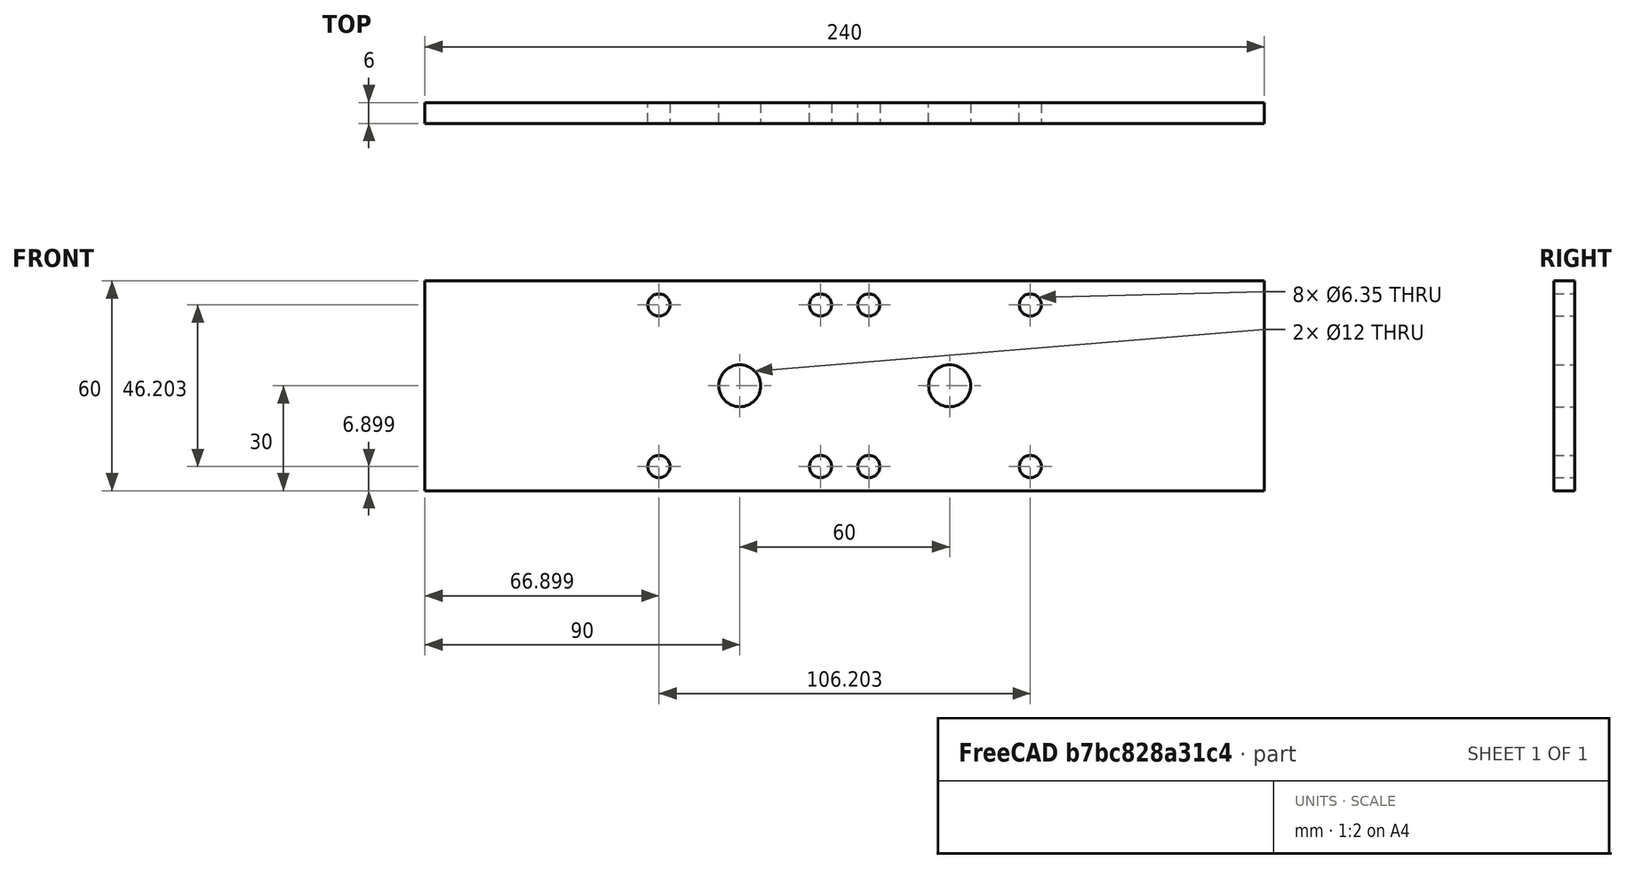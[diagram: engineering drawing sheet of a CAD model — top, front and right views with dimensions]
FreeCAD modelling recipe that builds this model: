
FCSTD DOCUMENT  (FreeCAD 0.18R4 (GitTag))
Label: soporte_motor
License: All rights reserved
LicenseURL: http://en.wikipedia.org/wiki/All_rights_reserved
objects: Sketcher::SketchObject×1, PartDesign::Pad×1, PartDesign::Body×1
note: 4 computed .brp shape members not serialized (recipe doc carries the construction recipe); baked Part::Feature solids carry a one-line shape summary decoded from their .brp

FEATURE [Sketcher::SketchObject] Sketch
  MapMode = 5
  Placement = pos=(0,0,0) rot=(1,0,0;1.5708rad)
  Support = -> [XZ_Plane]
  sketch-geometry (14):
    g0: LineSegment StartX=0 StartY=0 StartZ=0 EndX=240 EndY=0 EndZ=0
    g1: LineSegment StartX=240 StartY=0 StartZ=0 EndX=240 EndY=60 EndZ=0
    g2: LineSegment StartX=240 StartY=60 StartZ=0 EndX=0 EndY=60 EndZ=0
    g3: LineSegment StartX=0 StartY=60 StartZ=0 EndX=0 EndY=0 EndZ=0
    g4: Circle CenterX=90 CenterY=30 CenterZ=0 NormalX=0 NormalY=0 NormalZ=1 AngleXU=0 Radius=6
    g5: Circle CenterX=113.101 CenterY=53.1013 CenterZ=0 NormalX=0 NormalY=0 NormalZ=1 AngleXU=0 Radius=3.175
    g6: Circle CenterX=66.8987 CenterY=53.1013 CenterZ=0 NormalX=0 NormalY=0 NormalZ=1 AngleXU=0 Radius=3.175
    g7: Circle CenterX=66.8987 CenterY=6.8987 CenterZ=0 NormalX=0 NormalY=0 NormalZ=1 AngleXU=0 Radius=3.175
    g8: Circle CenterX=113.101 CenterY=6.8987 CenterZ=0 NormalX=0 NormalY=0 NormalZ=1 AngleXU=0 Radius=3.175
    g9: Circle CenterX=150 CenterY=30 CenterZ=0 NormalX=0 NormalY=0 NormalZ=1 AngleXU=0 Radius=6
    g10: Circle CenterX=173.101 CenterY=53.1013 CenterZ=0 NormalX=0 NormalY=0 NormalZ=1 AngleXU=0 Radius=3.175
    g11: Circle CenterX=126.899 CenterY=53.1013 CenterZ=0 NormalX=0 NormalY=0 NormalZ=1 AngleXU=0 Radius=3.175
    g12: Circle CenterX=126.899 CenterY=6.8987 CenterZ=0 NormalX=0 NormalY=0 NormalZ=1 AngleXU=0 Radius=3.175
    g13: Circle CenterX=173.101 CenterY=6.8987 CenterZ=0 NormalX=0 NormalY=0 NormalZ=1 AngleXU=0 Radius=3.175
  constraints (41):
    c: Coincident(g0,g1)
    c: Coincident(g1,g2)
    c: Coincident(g2,g3)
    c: Coincident(g3,g0)
    c: Horizontal(g0)
    c: Horizontal(g2)
    c: Vertical(g1)
    c: Vertical(g3)
    c: Coincident(g0,g-1)
    c: DistanceX(g0,g0) = 240
    c: DistanceY(g3,g3) = 60
    c: Distance(g4,g2) = 30
    c: Distance(g4,g3) = 90
    c: Radius(g4) = 6
    c: Radius(g5) = 3.175
    c: Radius(g6) = 3.175
    c: Radius(g8) = 3.175
    c: Radius(g7) = 3.175
    c: DistanceX(g7,g8) = 46.2026
    c: DistanceX(g6,g5) = 46.2026
    c: DistanceX(g6,g4) = 23.1013
    c: DistanceX(g7,g4) = 23.1013
    c: DistanceY(g8,g5) = 46.2026
    c: DistanceY(g8,g4) = 23.1013
    c: DistanceY(g7,g6) = 46.2026
    c: DistanceY(g4,g6) = 23.1013
    c: Equal(g4,g9) = 6
    c: Equal(g5,g10) = 3.175
    c: Equal(g6,g11) = 3.175
    c: Equal(g8,g13) = 3.175
    c: Equal(g7,g12) = 3.175
    c: DistanceX(g12,g13) = 46.2026
    c: DistanceX(g11,g10) = 46.2026
    c: DistanceX(g11,g9) = 23.1013
    c: DistanceX(g12,g9) = 23.1013
    c: DistanceY(g13,g10) = 46.2026
    c: DistanceY(g13,g9) = 23.1013
    c: DistanceY(g12,g11) = 46.2026
    c: DistanceY(g9,g11) = 23.1013
    c: Distance(g9,g3) = 150
    c: Distance(g9,g2) = 30
FEATURE [PartDesign::Pad] Pad
  Length = 6
  Length2 = 100
  Placement = pos=(0,0,0) rot=(1,0,0;1.5708rad)
  Profile = -> Sketch
  Type = 0
FEATURE [PartDesign::Body] Body
  Group = -> [Sketch,Pad]
  Origin = -> Origin
  Tip = -> Pad
